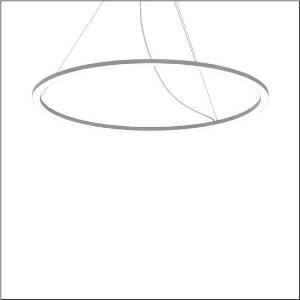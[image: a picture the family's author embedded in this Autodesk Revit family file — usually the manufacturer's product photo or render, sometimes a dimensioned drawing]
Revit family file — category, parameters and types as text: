
# Revit family: silica_r__21_ring-d_5pjbd4d1204a_bd2d
name_source: partatom
category: Lighting Fixtures
units: mm (PartAtom-declared; Revit-internal decimal feet)

## family parameters
Cut with Voids When Loaded = No
Host = Face
Light Source = No
Part Type = Normal
Room Calculation Point = No
Round Connector Dimension = Use Diameter
Shared = No

## types (1)
- Silica® 21 Ring-D (1 x LED, 10840 lm, 125 W, 3000K)
    Apparent Load = 125 VA
    CIE Flux Codes = 37 69 92 100 100
    Color Rendering = 80
    Color Temperature = 3000K
    Default Elevation = 1800 mm
    Description = Silica® 21 Ring-D, suspended luminaire, of PMMA, frosted, light emission: ring underside luminous distribution, primary light characteristic: symmetric, installation type: suspended mounting, LED, rated luminous flux: 10.840lm, luminous efficacy: 87lm/W, light colour: 830, colour temperature: 3000K, with terminal, 5-pole, mains connection: 230V, AC/DC, 0/50..60Hz, rated input power: 125W, housing, of extruded aluminium section, metallic grey (RAL 9006), diameter: 1.450mm, ceiling canopy, metallic grey (RAL 9006), protection rating (lamp compartment): IP40, insulation class (complete): insulation class I (protective earthing), certification: CE, impact resistance: IK02, permissible operating ambient temperature: 0..+35°C, packaging unit: 1 piece
    Height = 25 mm  [stored 0.082021 ft]
    Lamp = 1 x LED
    Lamp Light Flux = 10840 lm
    Lamp Power = 125 W
    Lamp count = 1
    Length = 1450 mm
    Luminous efficacy = 87 lm/W
    Manufacturer = Siteco
    ModVariant = No
    Model = 5PJBD4D1204A
    Mounting Place = Ceiling
    Mounting Type = Pendant
    Number of Poles = 1
    OnlyDefault = Yes
    Power Factor = 1
    Product Name = Silica® 21 Ring-D
    Product group = suspended luminaire
    ProductGroupID = 904
    Protection Class = Protection class I
    Protection Degree = Degree of protection
    RLX_Detail_Level = 1
    RLX_Emergency_Light_Flux = 0 lm
    RLX_Emergency_Type = 0
    RLX_Emergency_Type_DB = No
    RlxData = <blob elided: 17925 chars, md5=f1e318b1>
    Socket = socket
    Standby Power = 0 W
    System Light Flux = 10840 lm
    System Power = 125 W
    Type Comments = Product without accessories
    Type Image = l_1251748.jpg
    URL = http://relux.com
    VarID = ---
    Voltage = 0 V
    Weight = 0.00 kg
    Width = 0 mm  [stored 0 ft]

note: [stored X ft] marks values corroborated as IEEE doubles in the binary element streams (Revit-internal decimal feet)

## geometry (parser evidence)
native form markers: Blend x4, Sweep x11
no freeform markers — native parametric forms only
